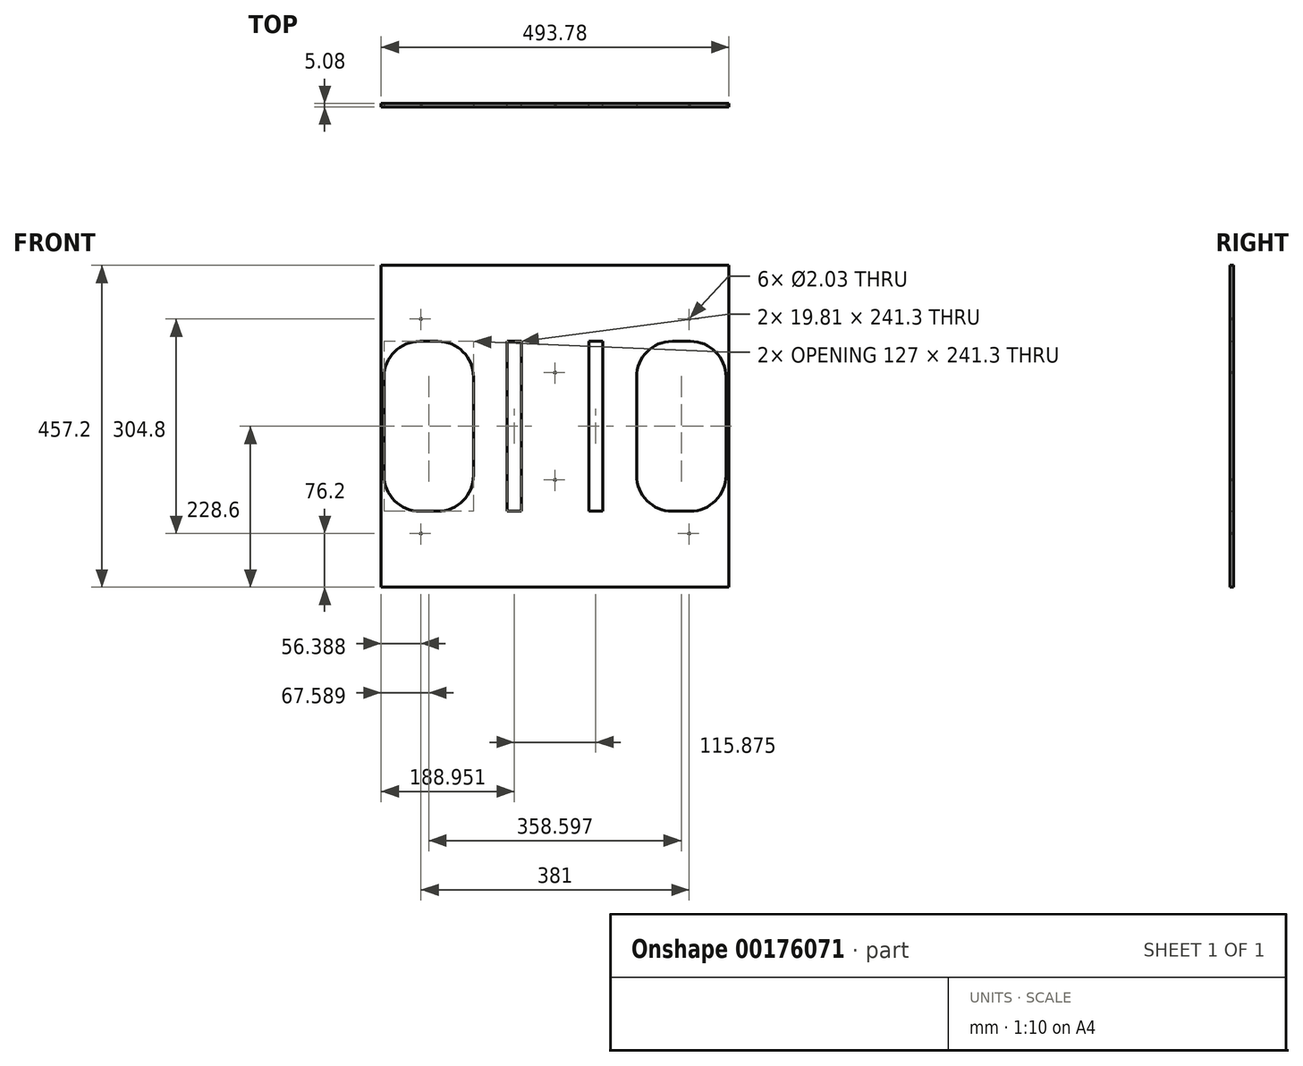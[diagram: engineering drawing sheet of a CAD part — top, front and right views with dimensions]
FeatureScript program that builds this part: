
annotation { "Feature Type Name" : "Feature", "Feature Type Description" : "" }
export const myFeature = defineFeature(function(context is Context, id is Id, definition is map)
    precondition{}
    {
        {
            var Q0;
            Q0=qCreatedBy(makeId("Front.planeOp"),FACE);
            var sketch = newSketch(context, id + "F0", { "sketchPlane" : qUnion([Q0])});
            skLineSegment(sketch, "E0.bottom", {"start": v(0, 0) * mm, "end": v(493.78, 0) * mm});
            skLineSegment(sketch, "E0.top", {"start": v(0, 457.2) * mm, "end": v(493.78, 457.2) * mm});
            skLineSegment(sketch, "E0.left", {"start": v(0, 0) * mm, "end": v(0, 457.2) * mm});
            skLineSegment(sketch, "E0.right", {"start": v(493.78, 0) * mm, "end": v(493.78, 457.2) * mm});
            skCircle(sketch, "E1.cCircle", {"center": v(101.7, 228.6) * mm, "radius": 125.73 * mm, "construction": true});
            skLineSegment(sketch, "E1.0", {"start": v(174.3, 354.33) * mm, "end": v(246.89, 228.6) * mm, "construction": true});
            skLineSegment(sketch, "E1.1", {"start": v(246.89, 228.6) * mm, "end": v(174.3, 102.87) * mm, "construction": true});
            skLineSegment(sketch, "E1.2", {"start": v(174.3, 102.87) * mm, "end": v(43.78, 102.87) * mm, "construction": true});
            skLineSegment(sketch, "E1.3", {"start": v(21.78, 115.57) * mm, "end": v(-36.14, 215.9) * mm, "construction": true});
            skLineSegment(sketch, "E1.4", {"start": v(-36.14, 241.3) * mm, "end": v(21.78, 341.63) * mm, "construction": true});
            skLineSegment(sketch, "E1.5", {"start": v(43.78, 354.33) * mm, "end": v(174.3, 354.33) * mm, "construction": true});
            skPoint(sketch, "E1.0.midPoint", {"position": v(210.6, 291.46) * mm});
            skCircle(sketch, "E2.cCircle", {"center": v(392.07, 228.6) * mm, "radius": 125.73 * mm, "construction": true});
            skLineSegment(sketch, "E2.0", {"start": v(472, 341.63) * mm, "end": v(529.92, 241.3) * mm, "construction": true});
            skLineSegment(sketch, "E2.1", {"start": v(529.92, 215.9) * mm, "end": v(472, 115.57) * mm, "construction": true});
            skLineSegment(sketch, "E2.2", {"start": v(450, 102.87) * mm, "end": v(319.48, 102.87) * mm, "construction": true});
            skLineSegment(sketch, "E2.3", {"start": v(319.48, 102.87) * mm, "end": v(246.89, 228.6) * mm, "construction": true});
            skLineSegment(sketch, "E2.4", {"start": v(246.89, 228.6) * mm, "end": v(319.48, 354.33) * mm, "construction": true});
            skLineSegment(sketch, "E2.5", {"start": v(319.48, 354.33) * mm, "end": v(450, 354.33) * mm, "construction": true});
            skPoint(sketch, "E2.0.midPoint", {"position": v(500.95, 291.46) * mm});
            skLineSegment(sketch, "E3", {"start": v(174.3, 354.33) * mm, "end": v(319.48, 354.33) * mm, "construction": true});
            skLineSegment(sketch, "E4", {"start": v(319.48, 102.87) * mm, "end": v(174.3, 102.87) * mm, "construction": true});
            skPoint(sketch, "E5.visualSharp", {"position": v(29.12, 354.33) * mm});
            skArc(sketch, "E5.filletArc", {"start": v(43.78, 354.33) * mm, "mid": v(31.08, 350.93) * mm, "end": v(21.78, 341.63) * mm, "construction": true});
            skPoint(sketch, "E6.visualSharp", {"position": v(-43.47, 228.6) * mm});
            skArc(sketch, "E6.filletArc", {"start": v(-36.14, 241.3) * mm, "mid": v(-39.54, 228.6) * mm, "end": v(-36.14, 215.9) * mm, "construction": true});
            skPoint(sketch, "E7.visualSharp", {"position": v(29.12, 102.87) * mm});
            skArc(sketch, "E7.filletArc", {"start": v(21.78, 115.57) * mm, "mid": v(31.08, 106.27) * mm, "end": v(43.78, 102.87) * mm, "construction": true});
            skPoint(sketch, "E8.visualSharp", {"position": v(464.66, 102.87) * mm});
            skArc(sketch, "E8.filletArc", {"start": v(450, 102.87) * mm, "mid": v(462.7, 106.27) * mm, "end": v(472, 115.57) * mm, "construction": true});
            skPoint(sketch, "E9.visualSharp", {"position": v(537.25, 228.6) * mm});
            skArc(sketch, "E9.filletArc", {"start": v(529.92, 215.9) * mm, "mid": v(533.32, 228.6) * mm, "end": v(529.92, 241.3) * mm, "construction": true});
            skPoint(sketch, "E10.visualSharp", {"position": v(464.66, 354.33) * mm});
            skArc(sketch, "E10.filletArc", {"start": v(472, 341.63) * mm, "mid": v(462.7, 350.93) * mm, "end": v(450, 354.33) * mm, "construction": true});
            skPoint(sketch, "E11", {"position": v(246.89, 457.2) * mm});
            skPoint(sketch, "E12", {"position": v(0, 228.6) * mm});
            skCircle(sketch, "E13.cCircle", {"center": v(246.89, 228.6) * mm, "radius": 125.73 * mm, "construction": true});
            skLineSegment(sketch, "E13.1", {"start": v(319.48, 354.33) * mm, "end": v(392.07, 228.6) * mm, "construction": true});
            skLineSegment(sketch, "E13.2", {"start": v(392.07, 228.6) * mm, "end": v(319.48, 102.87) * mm, "construction": true});
            skLineSegment(sketch, "E13.4", {"start": v(174.3, 102.87) * mm, "end": v(101.7, 228.6) * mm, "construction": true});
            skLineSegment(sketch, "E13.5", {"start": v(101.7, 228.6) * mm, "end": v(174.3, 354.33) * mm, "construction": true});
            skPoint(sketch, "E13.0.midPoint", {"position": v(246.89, 354.33) * mm});
            skLineSegment(sketch, "E14.bottom", {"start": v(179.04, 349.25) * mm, "end": v(198.86, 349.25) * mm});
            skLineSegment(sketch, "E14.top", {"start": v(179.04, 107.95) * mm, "end": v(198.86, 107.95) * mm});
            skLineSegment(sketch, "E14.left", {"start": v(179.04, 349.25) * mm, "end": v(179.04, 107.95) * mm});
            skLineSegment(sketch, "E14.right", {"start": v(198.86, 349.25) * mm, "end": v(198.86, 107.95) * mm});
            skLineSegment(sketch, "E15", {"start": v(188.95, 349.25) * mm, "end": v(188.95, 107.95) * mm, "construction": true});
            skPoint(sketch, "E16", {"position": v(188.95, 228.6) * mm});
            skLineSegment(sketch, "E17", {"start": v(246.89, 228.6) * mm, "end": v(246.89, 281.64) * mm, "construction": true});
            skLineSegment(sketch, "E18.MirrorCS", {"start": v(314.73, 107.95) * mm, "end": v(294.92, 107.95) * mm});
            skLineSegment(sketch, "E19.MirrorCS", {"start": v(294.92, 349.25) * mm, "end": v(294.92, 107.95) * mm});
            skLineSegment(sketch, "E20.MirrorCS", {"start": v(314.73, 349.25) * mm, "end": v(294.92, 349.25) * mm});
            skLineSegment(sketch, "E21.MirrorCS", {"start": v(314.73, 349.25) * mm, "end": v(314.73, 107.95) * mm});
            skSolve(sketch);
        }
        {
            var Q0;
            Q0 = qSketchRegion(id + "F0", true);
            extrude(context, id + "F1", {"entities" : qUnion([Q0]), "depth" : 5.08 * mm});
        }
        {
            var Q0;
            Q0=makeQuery(id+"F1.opExtrude","CAP_FACE",FACE,{"disambiguationData":[OSD([sQuery(id+"F0.wireOp",EDGE,"E0.bottom"),sQuery(id+"F0.wireOp",EDGE,"E0.top"),sQuery(id+"F0.wireOp",EDGE,"E0.left"),sQuery(id+"F0.wireOp",EDGE,"E0.right"),sQuery(id+"F0.wireOp",EDGE,"E14.bottom"),sQuery(id+"F0.wireOp",EDGE,"E14.top"),sQuery(id+"F0.wireOp",EDGE,"E14.left"),sQuery(id+"F0.wireOp",EDGE,"E14.right"),sQuery(id+"F0.wireOp",EDGE,"E18.MirrorCS"),sQuery(id+"F0.wireOp",EDGE,"E19.MirrorCS"),sQuery(id+"F0.wireOp",EDGE,"E20.MirrorCS"),sQuery(id+"F0.wireOp",EDGE,"E21.MirrorCS")])],"isStart":false});
            var sketch = newSketch(context, id + "F2", { "sketchPlane" : qUnion([Q0])});
            skCircle(sketch, "E22", {"center": v(56.39, 381) * mm, "radius": 1.02 * mm});
            skCircle(sketch, "E23", {"center": v(437.39, 381) * mm, "radius": 1.02 * mm});
            skCircle(sketch, "E24", {"center": v(56.39, 76.2) * mm, "radius": 1.02 * mm});
            skCircle(sketch, "E25", {"center": v(437.39, 76.2) * mm, "radius": 1.02 * mm});
            skLineSegment(sketch, "E26", {"start": v(-19.81, 457.2) * mm, "end": v(-19.81, 0) * mm, "construction": true});
            skLineSegment(sketch, "E27", {"start": v(513.59, 0) * mm, "end": v(513.59, 457.2) * mm, "construction": true});
            skCircle(sketch, "E28", {"center": v(246.89, 304.8) * mm, "radius": 1.02 * mm});
            skCircle(sketch, "E29", {"center": v(246.89, 152.4) * mm, "radius": 1.02 * mm});
            skLineSegment(sketch, "E30", {"start": v(246.89, 304.8) * mm, "end": v(246.89, 152.4) * mm, "construction": true});
            skPoint(sketch, "E31", {"position": v(246.89, 228.6) * mm});
            skSolve(sketch);
        }
        {
            var Q0;
            Q0=makeQuery(id+"F2.imprint","IMPRINT",FACE,{"disambiguationData":[TD([[makeQuery(id+"F2.imprint","IMPRINT",EDGE,{"derivedFrom":sQuery(id+"F2.wireOp",EDGE,"H294jyfB-SMhl-eZz6-ISZu-JyYH6zuhgEUc")}),1.0]])]});
            var Q1;
            Q1=makeQuery(id+"F2.imprint","IMPRINT",FACE,{"disambiguationData":[TD([[makeQuery(id+"F2.imprint","IMPRINT",EDGE,{"derivedFrom":sQuery(id+"F2.wireOp",EDGE,"c7ec66d4-dd6e-4ef9-a3be-b1267b95481f.1.0.0")}),1.0]])]});
            var Q2;
            Q2=makeQuery(id+"F2.imprint","IMPRINT",FACE,{"disambiguationData":[TD([[makeQuery(id+"F2.imprint","IMPRINT",EDGE,{"derivedFrom":sQuery(id+"F2.wireOp",EDGE,"c7ec66d4-dd6e-4ef9-a3be-b1267b95481f.1.1.0")}),1.0]])]});
            var Q3;
            Q3=makeQuery(id+"F2.imprint","IMPRINT",FACE,{"disambiguationData":[TD([[makeQuery(id+"F2.imprint","IMPRINT",EDGE,{"derivedFrom":sQuery(id+"F2.wireOp",EDGE,"c7ec66d4-dd6e-4ef9-a3be-b1267b95481f.0.1.0")}),1.0]])]});
            var Q4;
            Q4=makeQuery(id+"F2.imprint","IMPRINT",FACE,{"disambiguationData":[TD([[makeQuery(id+"F2.imprint","IMPRINT",EDGE,{"derivedFrom":sQuery(id+"F2.wireOp",EDGE,"E22")}),1.0]])]});
            var Q5;
            Q5=makeQuery(id+"F2.imprint","IMPRINT",FACE,{"disambiguationData":[TD([[makeQuery(id+"F2.imprint","IMPRINT",EDGE,{"derivedFrom":sQuery(id+"F2.wireOp",EDGE,"E24")}),1.0]])]});
            var Q6;
            Q6=makeQuery(id+"F2.imprint","IMPRINT",FACE,{"disambiguationData":[TD([[makeQuery(id+"F2.imprint","IMPRINT",EDGE,{"derivedFrom":sQuery(id+"F2.wireOp",EDGE,"E25")}),1.0]])]});
            var Q7;
            Q7=makeQuery(id+"F2.imprint","IMPRINT",FACE,{"disambiguationData":[TD([[makeQuery(id+"F2.imprint","IMPRINT",EDGE,{"derivedFrom":sQuery(id+"F2.wireOp",EDGE,"E23")}),1.0]])]});
            extrude(context, id + "F3", {"entities" : qUnion([Q0, Q1, Q2, Q3, Q4, Q5, Q6, Q7]), "operationType" : NewBodyOperationType.REMOVE, "endBound" : BoundingType.THROUGH_ALL, "oppositeDirection" : true, "depth" : 25.4 * mm});
        }
        {
            var Q0;
            Q0=makeQuery(id+"F1.opExtrude","CAP_FACE",FACE,{"disambiguationData":[OSD([sQuery(id+"F0.wireOp",EDGE,"E0.bottom"),sQuery(id+"F0.wireOp",EDGE,"E0.top"),sQuery(id+"F0.wireOp",EDGE,"E0.left"),sQuery(id+"F0.wireOp",EDGE,"E0.right"),sQuery(id+"F0.wireOp",EDGE,"E14.bottom"),sQuery(id+"F0.wireOp",EDGE,"E14.top"),sQuery(id+"F0.wireOp",EDGE,"E14.left"),sQuery(id+"F0.wireOp",EDGE,"E14.right"),sQuery(id+"F0.wireOp",EDGE,"E18.MirrorCS"),sQuery(id+"F0.wireOp",EDGE,"E19.MirrorCS"),sQuery(id+"F0.wireOp",EDGE,"E20.MirrorCS"),sQuery(id+"F0.wireOp",EDGE,"E21.MirrorCS")])],"isStart":false});
            var sketch = newSketch(context, id + "F4", { "sketchPlane" : qUnion([Q0])});
            skLineSegment(sketch, "E32.bottom", {"start": v(54.89, 349.25) * mm, "end": v(80.29, 349.25) * mm});
            skLineSegment(sketch, "E32.top", {"start": v(54.89, 107.95) * mm, "end": v(80.29, 107.95) * mm});
            skLineSegment(sketch, "E32.left", {"start": v(4.09, 298.45) * mm, "end": v(4.09, 158.75) * mm});
            skLineSegment(sketch, "E32.right", {"start": v(131.09, 298.45) * mm, "end": v(131.09, 158.75) * mm});
            skLineSegment(sketch, "E33.bottom", {"start": v(413.49, 349.25) * mm, "end": v(438.89, 349.25) * mm});
            skLineSegment(sketch, "E33.top", {"start": v(413.49, 107.95) * mm, "end": v(438.89, 107.95) * mm});
            skLineSegment(sketch, "E33.left", {"start": v(362.69, 298.45) * mm, "end": v(362.69, 158.75) * mm});
            skLineSegment(sketch, "E33.right", {"start": v(489.69, 298.45) * mm, "end": v(489.69, 158.75) * mm});
            skLineSegment(sketch, "E34", {"start": v(67.59, 349.25) * mm, "end": v(67.59, 107.95) * mm, "construction": true});
            skLineSegment(sketch, "E35", {"start": v(426.19, 349.25) * mm, "end": v(426.19, 107.95) * mm, "construction": true});
            skPoint(sketch, "E36.visualSharp", {"position": v(4.09, 349.25) * mm});
            skArc(sketch, "E36.filletArc", {"start": v(54.89, 349.25) * mm, "mid": v(18.97, 334.37) * mm, "end": v(4.09, 298.45) * mm});
            skPoint(sketch, "E37.visualSharp", {"position": v(131.09, 349.25) * mm});
            skArc(sketch, "E37.filletArc", {"start": v(131.09, 298.45) * mm, "mid": v(116.21, 334.37) * mm, "end": v(80.29, 349.25) * mm});
            skPoint(sketch, "E38.visualSharp", {"position": v(4.09, 107.95) * mm});
            skArc(sketch, "E38.filletArc", {"start": v(4.09, 158.75) * mm, "mid": v(18.97, 122.83) * mm, "end": v(54.89, 107.95) * mm});
            skPoint(sketch, "E39.visualSharp", {"position": v(131.09, 107.95) * mm});
            skArc(sketch, "E39.filletArc", {"start": v(80.29, 107.95) * mm, "mid": v(116.21, 122.83) * mm, "end": v(131.09, 158.75) * mm});
            skPoint(sketch, "E40.visualSharp", {"position": v(362.69, 349.25) * mm});
            skArc(sketch, "E40.filletArc", {"start": v(413.49, 349.25) * mm, "mid": v(377.57, 334.37) * mm, "end": v(362.69, 298.45) * mm});
            skPoint(sketch, "E41.visualSharp", {"position": v(489.69, 349.25) * mm});
            skArc(sketch, "E41.filletArc", {"start": v(489.69, 298.45) * mm, "mid": v(474.8, 334.37) * mm, "end": v(438.89, 349.25) * mm});
            skPoint(sketch, "E42.visualSharp", {"position": v(362.69, 107.95) * mm});
            skArc(sketch, "E42.filletArc", {"start": v(362.69, 158.75) * mm, "mid": v(377.57, 122.83) * mm, "end": v(413.49, 107.95) * mm});
            skPoint(sketch, "E43.visualSharp", {"position": v(489.69, 107.95) * mm});
            skArc(sketch, "E43.filletArc", {"start": v(438.89, 107.95) * mm, "mid": v(474.8, 122.83) * mm, "end": v(489.69, 158.75) * mm});
            skSolve(sketch);
        }
        {
            var Q0;
            Q0=makeQuery(id+"F4.imprint","IMPRINT",FACE,{"disambiguationData":[TD([[makeQuery(id+"F4.imprint","IMPRINT",EDGE,{"derivedFrom":sQuery(id+"F4.wireOp",EDGE,"E32.bottom")}),-1.0]])]});
            var Q1;
            Q1=makeQuery(id+"F4.imprint","IMPRINT",FACE,{"disambiguationData":[TD([[makeQuery(id+"F4.imprint","IMPRINT",EDGE,{"derivedFrom":sQuery(id+"F4.wireOp",EDGE,"E33.bottom")}),-1.0]])]});
            extrude(context, id + "F5", {"entities" : qUnion([Q0, Q1]), "operationType" : NewBodyOperationType.REMOVE, "endBound" : BoundingType.THROUGH_ALL, "oppositeDirection" : true, "depth" : 25.4 * mm});
        }
        {
            var Q0;
            Q0=makeQuery(id+"F2.imprint","IMPRINT",FACE,{"disambiguationData":[TD([[makeQuery(id+"F2.imprint","IMPRINT",EDGE,{"derivedFrom":sQuery(id+"F2.wireOp",EDGE,"E28")}),1.0]])]});
            var Q1;
            Q1=makeQuery(id+"F2.imprint","IMPRINT",FACE,{"disambiguationData":[TD([[makeQuery(id+"F2.imprint","IMPRINT",EDGE,{"derivedFrom":sQuery(id+"F2.wireOp",EDGE,"E29")}),1.0]])]});
            var Q2;
            Q2=makeQuery(id+"F1.opExtrude","CAP_FACE",FACE,{"disambiguationData":[OSD([sQuery(id+"F0.wireOp",EDGE,"E0.bottom"),sQuery(id+"F0.wireOp",EDGE,"E0.top"),sQuery(id+"F0.wireOp",EDGE,"E0.left"),sQuery(id+"F0.wireOp",EDGE,"E0.right"),sQuery(id+"F0.wireOp",EDGE,"E14.bottom"),sQuery(id+"F0.wireOp",EDGE,"E14.top"),sQuery(id+"F0.wireOp",EDGE,"E14.left"),sQuery(id+"F0.wireOp",EDGE,"E14.right"),sQuery(id+"F0.wireOp",EDGE,"E18.MirrorCS"),sQuery(id+"F0.wireOp",EDGE,"E19.MirrorCS"),sQuery(id+"F0.wireOp",EDGE,"E20.MirrorCS"),sQuery(id+"F0.wireOp",EDGE,"E21.MirrorCS")])],"isStart":true});
            extrude(context, id + "F6", {"entities" : qUnion([Q0, Q1]), "operationType" : NewBodyOperationType.REMOVE, "endBound" : BoundingType.UP_TO_SURFACE, "oppositeDirection" : true, "endBoundEntityFace" : qUnion([Q2]), "depth" : 25.4 * mm});
        }
    });
